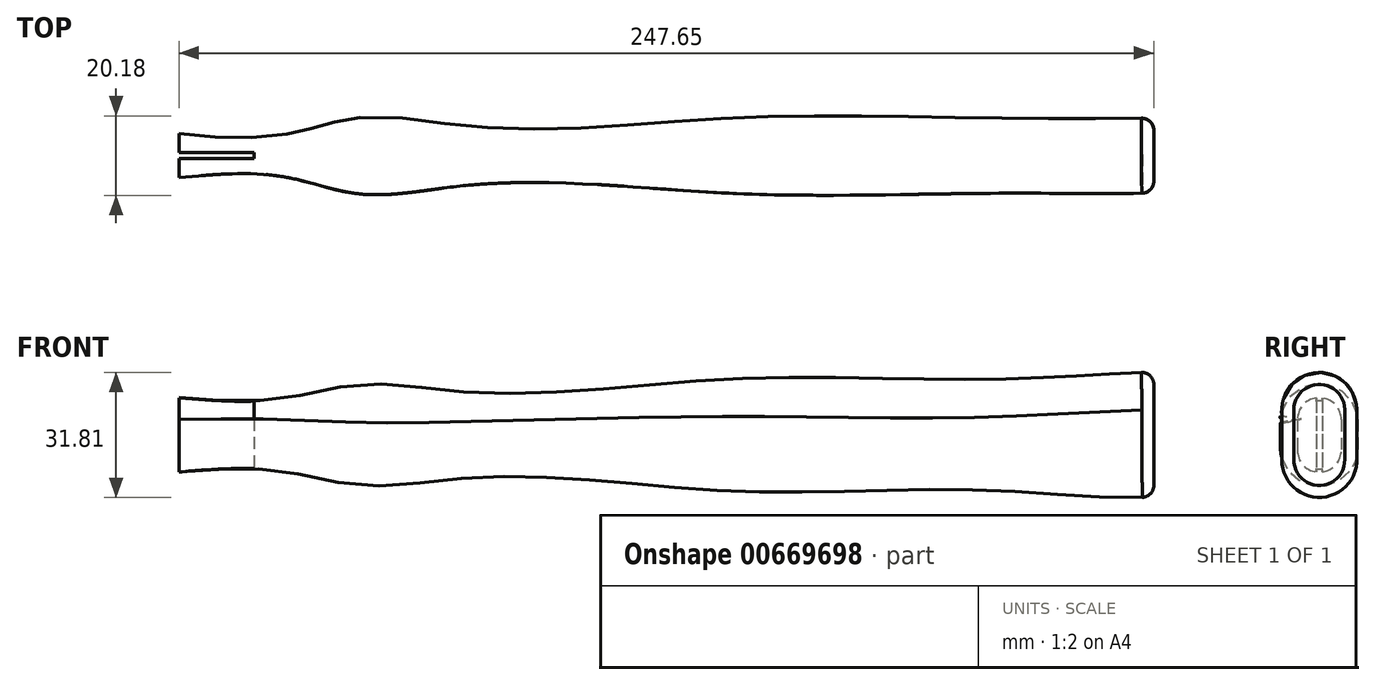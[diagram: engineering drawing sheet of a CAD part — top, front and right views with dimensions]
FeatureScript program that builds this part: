
annotation { "Feature Type Name" : "Feature", "Feature Type Description" : "" }
export const myFeature = defineFeature(function(context is Context, id is Id, definition is map)
    precondition{}
    {
        {
            var Q0;
            Q0=qCreatedBy(makeId("Right.planeOp"),FACE);
            var sketch = newSketch(context, id + "F0", { "sketchPlane" : qUnion([Q0])});
            skLineSegment(sketch, "E0.left", {"start": v(-5.59, 3.87) * mm, "end": v(-5.59, -3.87) * mm});
            skLineSegment(sketch, "E0.right", {"start": v(5.59, 3.87) * mm, "end": v(5.59, -3.87) * mm});
            skPoint(sketch, "E0.middle", {"position": v(0, 0) * mm});
            skLineSegment(sketch, "E1", {"start": v(0, 9.46) * mm, "end": v(0, -9.46) * mm, "construction": true});
            skLineSegment(sketch, "E2", {"start": v(-5.59, 0) * mm, "end": v(5.59, 0) * mm, "construction": true});
            skArc(sketch, "E3", {"start": v(5.59, 3.87) * mm, "mid": v(0, 9.46) * mm, "end": v(-5.59, 3.87) * mm});
            skArc(sketch, "E4.MirrorCS", {"start": v(5.59, -3.87) * mm, "mid": v(0, -9.46) * mm, "end": v(-5.59, -3.87) * mm});
            skSolve(sketch);
        }
        {
            var Q0;
            Q0=qCreatedBy(makeId("Right.planeOp"),FACE);
            cPlane(context, id + "F1", {"entities" : qUnion([Q0]), "cplaneType" : CPlaneType.OFFSET, "offset" : 27.94 * mm, "width" : 152.4 * mm, "height" : 152.4 * mm});
        }
        {
            var Q0;
            Q0=qCreatedBy(id+"F1.planeOp",FACE);
            var sketch = newSketch(context, id + "F2", { "sketchPlane" : qUnion([Q0])});
            skLineSegment(sketch, "E5.left", {"start": v(-5.59, 3.87) * mm, "end": v(-5.59, -3.87) * mm});
            skLineSegment(sketch, "E5.right", {"start": v(5.59, 3.87) * mm, "end": v(5.59, -3.87) * mm});
            skPoint(sketch, "E5.middle", {"position": v(0, 0) * mm});
            skLineSegment(sketch, "E6", {"start": v(0, 9.46) * mm, "end": v(0, -9.46) * mm, "construction": true});
            skLineSegment(sketch, "E7", {"start": v(-5.59, 0) * mm, "end": v(5.59, 0) * mm, "construction": true});
            skArc(sketch, "E8", {"start": v(5.59, 3.87) * mm, "mid": v(0, 9.46) * mm, "end": v(-5.59, 3.87) * mm});
            skArc(sketch, "E9.MirrorCS", {"start": v(5.59, -3.87) * mm, "mid": v(0, -9.46) * mm, "end": v(-5.59, -3.87) * mm});
            skSolve(sketch);
        }
        {
            var Q0;
            Q0=qCreatedBy(makeId("Right.planeOp"),FACE);
            cPlane(context, id + "F3", {"entities" : qUnion([Q0]), "cplaneType" : CPlaneType.OFFSET, "offset" : 44.45 * mm, "width" : 152.4 * mm, "height" : 152.4 * mm});
        }
        {
            var Q0;
            Q0=qCreatedBy(id+"F3.planeOp",FACE);
            var sketch = newSketch(context, id + "F4", { "sketchPlane" : qUnion([Q0])});
            skLineSegment(sketch, "E10.left", {"start": v(-9.53, 3.17) * mm, "end": v(-9.52, -3.18) * mm});
            skLineSegment(sketch, "E10.right", {"start": v(9.53, 3.18) * mm, "end": v(9.53, -3.17) * mm});
            skPoint(sketch, "E10.middle", {"position": v(0, 0) * mm});
            skLineSegment(sketch, "E11", {"start": v(0, 12.7) * mm, "end": v(0, -12.7) * mm, "construction": true});
            skLineSegment(sketch, "E12", {"start": v(-9.53, 0) * mm, "end": v(9.53, 0) * mm, "construction": true});
            skArc(sketch, "E13", {"start": v(9.53, 3.18) * mm, "mid": v(0, 12.7) * mm, "end": v(-9.53, 3.17) * mm});
            skArc(sketch, "E14.MirrorCS", {"start": v(9.53, -3.17) * mm, "mid": v(0, -12.7) * mm, "end": v(-9.52, -3.18) * mm});
            skSolve(sketch);
        }
        {
            var Q0;
            Q0=qCreatedBy(makeId("Right.planeOp"),FACE);
            cPlane(context, id + "F5", {"entities" : qUnion([Q0]), "cplaneType" : CPlaneType.OFFSET, "offset" : 69.85 * mm, "width" : 152.4 * mm, "height" : 152.4 * mm});
        }
        {
            var Q0;
            Q0=qCreatedBy(id+"F5.planeOp",FACE);
            var sketch = newSketch(context, id + "F6", { "sketchPlane" : qUnion([Q0])});
            skLineSegment(sketch, "E15.left", {"start": v(-7.87, 3.3) * mm, "end": v(-7.87, -3.3) * mm});
            skLineSegment(sketch, "E15.right", {"start": v(7.87, 3.3) * mm, "end": v(7.87, -3.3) * mm});
            skPoint(sketch, "E15.middle", {"position": v(0, 0) * mm});
            skLineSegment(sketch, "E16", {"start": v(0, 11.18) * mm, "end": v(0, -11.18) * mm, "construction": true});
            skLineSegment(sketch, "E17", {"start": v(-7.87, 0) * mm, "end": v(7.87, 0) * mm, "construction": true});
            skArc(sketch, "E18", {"start": v(7.87, 3.3) * mm, "mid": v(0, 11.18) * mm, "end": v(-7.87, 3.3) * mm});
            skArc(sketch, "E19.MirrorCS", {"start": v(7.87, -3.3) * mm, "mid": v(0, -11.18) * mm, "end": v(-7.87, -3.3) * mm});
            skSolve(sketch);
        }
        {
            var Q0;
            Q0=qCreatedBy(makeId("Right.planeOp"),FACE);
            cPlane(context, id + "F7", {"entities" : qUnion([Q0]), "cplaneType" : CPlaneType.OFFSET, "offset" : 139.7 * mm, "width" : 152.4 * mm, "height" : 152.4 * mm});
        }
        {
            var Q0;
            Q0=qCreatedBy(id+"F7.planeOp",FACE);
            var sketch = newSketch(context, id + "F8", { "sketchPlane" : qUnion([Q0])});
            skLineSegment(sketch, "E20.left", {"start": v(-9.52, 4.7) * mm, "end": v(-9.52, -4.7) * mm});
            skLineSegment(sketch, "E20.right", {"start": v(9.53, 4.7) * mm, "end": v(9.53, -4.7) * mm});
            skPoint(sketch, "E20.middle", {"position": v(0, 0) * mm});
            skLineSegment(sketch, "E21", {"start": v(0, 14.22) * mm, "end": v(0, -14.22) * mm, "construction": true});
            skLineSegment(sketch, "E22", {"start": v(-9.53, 0) * mm, "end": v(9.53, 0) * mm, "construction": true});
            skArc(sketch, "E23", {"start": v(9.53, 4.7) * mm, "mid": v(0, 14.22) * mm, "end": v(-9.52, 4.7) * mm});
            skArc(sketch, "E24.MirrorCS", {"start": v(9.53, -4.7) * mm, "mid": v(0, -14.22) * mm, "end": v(-9.52, -4.7) * mm});
            skSolve(sketch);
        }
        {
            var Q0;
            Q0=qCreatedBy(makeId("Right.planeOp"),FACE);
            cPlane(context, id + "F9", {"entities" : qUnion([Q0]), "cplaneType" : CPlaneType.OFFSET, "offset" : 209.55 * mm, "width" : 152.4 * mm, "height" : 152.4 * mm});
        }
        {
            var Q0;
            Q0=qCreatedBy(id+"F9.planeOp",FACE);
            var sketch = newSketch(context, id + "F10", { "sketchPlane" : qUnion([Q0])});
            skLineSegment(sketch, "E25.left", {"start": v(-9.53, 4.7) * mm, "end": v(-9.52, -4.7) * mm});
            skLineSegment(sketch, "E25.right", {"start": v(9.53, 4.7) * mm, "end": v(9.53, -4.7) * mm});
            skPoint(sketch, "E25.middle", {"position": v(0, 0) * mm});
            skLineSegment(sketch, "E26", {"start": v(0, 14.22) * mm, "end": v(0, -14.22) * mm, "construction": true});
            skLineSegment(sketch, "E27", {"start": v(-9.53, 0) * mm, "end": v(9.53, 0) * mm, "construction": true});
            skArc(sketch, "E28", {"start": v(9.53, 4.7) * mm, "mid": v(0, 14.22) * mm, "end": v(-9.53, 4.7) * mm});
            skArc(sketch, "E29.MirrorCS", {"start": v(9.53, -4.7) * mm, "mid": v(0, -14.22) * mm, "end": v(-9.53, -4.7) * mm});
            skSolve(sketch);
        }
        {
            var Q0;
            Q0=qCreatedBy(makeId("Right.planeOp"),FACE);
            cPlane(context, id + "F11", {"entities" : qUnion([Q0]), "cplaneType" : CPlaneType.OFFSET, "offset" : 244.6 * mm, "width" : 152.4 * mm, "height" : 152.4 * mm});
        }
        {
            var Q0;
            Q0=qCreatedBy(id+"F11.planeOp",FACE);
            var sketch = newSketch(context, id + "F12", { "sketchPlane" : qUnion([Q0])});
            skLineSegment(sketch, "E30.left", {"start": v(-9.52, 6.35) * mm, "end": v(-9.52, -6.35) * mm});
            skLineSegment(sketch, "E30.right", {"start": v(9.53, 6.35) * mm, "end": v(9.53, -6.35) * mm});
            skPoint(sketch, "E30.middle", {"position": v(0, 0) * mm});
            skLineSegment(sketch, "E31", {"start": v(0, 15.88) * mm, "end": v(0, -15.88) * mm, "construction": true});
            skLineSegment(sketch, "E32", {"start": v(-9.53, 0) * mm, "end": v(9.53, 0) * mm, "construction": true});
            skArc(sketch, "E33", {"start": v(9.53, 6.35) * mm, "mid": v(0, 15.88) * mm, "end": v(-9.52, 6.35) * mm});
            skArc(sketch, "E34.MirrorCS", {"start": v(9.53, -6.35) * mm, "mid": v(0, -15.88) * mm, "end": v(-9.52, -6.35) * mm});
            skSolve(sketch);
        }
        {
            var Q0;
            Q0=qCreatedBy(makeId("Right.planeOp"),FACE);
            cPlane(context, id + "F13", {"entities" : qUnion([Q0]), "cplaneType" : CPlaneType.OFFSET, "offset" : 247.65 * mm, "width" : 152.4 * mm, "height" : 152.4 * mm});
        }
        {
            var Q0;
            Q0=qCreatedBy(id+"F13.planeOp",FACE);
            var sketch = newSketch(context, id + "F14", { "sketchPlane" : qUnion([Q0])});
            skLineSegment(sketch, "E35.left", {"start": v(-9.48, 6.46) * mm, "end": v(-9.48, -6.24) * mm});
            skLineSegment(sketch, "E35.right", {"start": v(9.57, 6.46) * mm, "end": v(9.57, -6.24) * mm});
            skPoint(sketch, "E35.middle", {"position": v(0.04, 0.11) * mm});
            skLineSegment(sketch, "E36", {"start": v(0.04, 15.99) * mm, "end": v(0.04, -15.76) * mm, "construction": true});
            skLineSegment(sketch, "E37", {"start": v(-9.48, 0.11) * mm, "end": v(9.57, 0.11) * mm, "construction": true});
            skArc(sketch, "E38", {"start": v(9.57, 6.46) * mm, "mid": v(0.04, 15.99) * mm, "end": v(-9.48, 6.46) * mm});
            skArc(sketch, "E39.MirrorCS", {"start": v(9.57, -6.24) * mm, "mid": v(0.04, -15.76) * mm, "end": v(-9.48, -6.24) * mm});
            skSolve(sketch);
        }
        {
            var Q0;
            Q0=qSketchRegion(id+"F0",true);
            var Q1;
            Q1=qSketchRegion(id+"F2",true);
            var Q2;
            Q2=qSketchRegion(id+"F4",true);
            var Q3;
            Q3=qSketchRegion(id+"F6",true);
            var Q4;
            Q4=qSketchRegion(id+"F8",true);
            var Q5;
            Q5=qSketchRegion(id+"F10",true);
            var Q6;
            Q6=qSketchRegion(id+"F12",true);
            var Q7;
            Q7=qSketchRegion(id+"F14",true);
            loft(context, id + "F15", {"sheetProfilesArray" : [{ "sheetProfileEntities" : qUnion([Q0]) }, { "sheetProfileEntities" : qUnion([Q1]) }, { "sheetProfileEntities" : qUnion([Q2]) }, { "sheetProfileEntities" : qUnion([Q3]) }, { "sheetProfileEntities" : qUnion([Q4]) }, { "sheetProfileEntities" : qUnion([Q5]) }, { "sheetProfileEntities" : qUnion([Q6]) }, { "sheetProfileEntities" : qUnion([Q7]) }]});
        }
        {
            var Q0;
            Q0=makeQuery(id+"F15.opLoft","MID_CAP_EDGE",EDGE,{"disambiguationData":[OSD([sQuery(id+"F14.wireOp",EDGE,"E35.left"),sQuery(id+"F14.wireOp",EDGE,"E35.right"),sQuery(id+"F14.wireOp",EDGE,"E38")])],"capPos":7.0});
            fillet(context, id + "F16", {"entities" : qUnion([Q0]), "radius" : 3.05 * mm, "tangentPropagation" : true, "allowEdgeOverflow" : false});
        }
        {
            var Q0;
            Q0=makeQuery(id+"F15.opLoft","CAP_FACE",FACE,{"disambiguationData":[OSD([makeQuery(id+"F0.imprint","IMPRINT",FACE,{"disambiguationData":[TD([[makeQuery(id+"F0.imprint","IMPRINT",EDGE,{"derivedFrom":sQuery(id+"F0.wireOp",EDGE,"E0.left")}),1.0]])]})])],"isStart":true});
            var sketch = newSketch(context, id + "F17", { "sketchPlane" : qUnion([Q0])});
            skLineSegment(sketch, "E40", {"start": v(-5.59, 0) * mm, "end": v(5.59, 0) * mm, "construction": true});
            skLineSegment(sketch, "E41.bottom", {"start": v(0.76, 10) * mm, "end": v(-0.76, 10) * mm});
            skLineSegment(sketch, "E41.top", {"start": v(0.76, -10) * mm, "end": v(-0.76, -10) * mm});
            skLineSegment(sketch, "E41.left", {"start": v(0.76, 10) * mm, "end": v(0.76, -10) * mm});
            skLineSegment(sketch, "E41.right", {"start": v(-0.76, 10) * mm, "end": v(-0.76, -10) * mm});
            skPoint(sketch, "E41.middle", {"position": v(0, 0) * mm});
            skSolve(sketch);
        }
        {
            var Q0;
            Q0=qSketchRegion(id+"F17",true);
            extrude(context, id + "F18", {"entities" : qUnion([Q0]), "operationType" : NewBodyOperationType.REMOVE, "oppositeDirection" : true, "depth" : 19.05 * mm, "offsetDistance" : 25.4 * mm});
        }
    });
